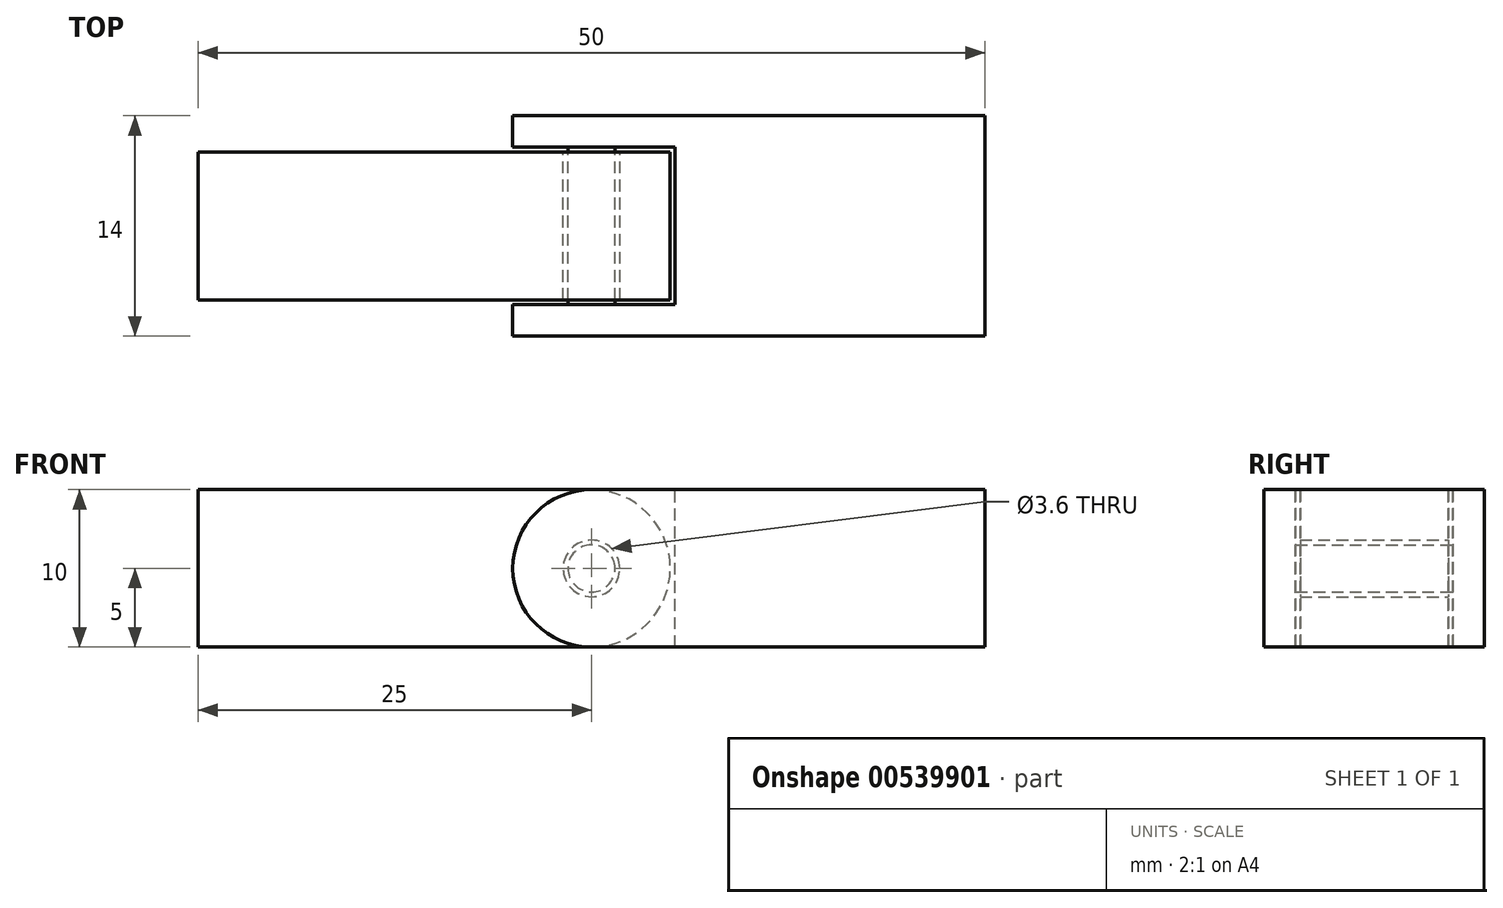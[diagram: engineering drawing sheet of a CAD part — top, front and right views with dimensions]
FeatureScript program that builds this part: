
annotation { "Feature Type Name" : "Feature", "Feature Type Description" : "" }
export const myFeature = defineFeature(function(context is Context, id is Id, definition is map)
    precondition{}
    {
        {
            var Q0;
            Q0=qCreatedBy(makeId("Front.planeOp"),FACE);
            var sketch = newSketch(context, id + "F0", { "sketchPlane" : qUnion([Q0])});
            skLineSegment(sketch, "E0.bottom", {"start": v(0, 0) * mm, "end": v(-25, 0) * mm});
            skLineSegment(sketch, "E0.top", {"start": v(0, 10) * mm, "end": v(-25, 10) * mm});
            skLineSegment(sketch, "E0.left", {"start": v(0, 0) * mm, "end": v(0, 10) * mm});
            skLineSegment(sketch, "E0.right", {"start": v(-30, 5) * mm, "end": v(-30, 5) * mm});
            skPoint(sketch, "E1.visualSharp", {"position": v(-30, 10) * mm});
            skArc(sketch, "E1.filletArc", {"start": v(-25, 10) * mm, "mid": v(-28.54, 8.54) * mm, "end": v(-30, 5) * mm});
            skPoint(sketch, "E2.visualSharp", {"position": v(-30, 0) * mm});
            skArc(sketch, "E2.filletArc", {"start": v(-30, 5) * mm, "mid": v(-28.54, 1.46) * mm, "end": v(-25, 0) * mm});
            skLineSegment(sketch, "E3", {"start": v(-30, 5) * mm, "end": v(-11.95, 5) * mm, "construction": true});
            skLineSegment(sketch, "E4", {"start": v(-25, 10) * mm, "end": v(-25, -3.08) * mm, "construction": true});
            skSolve(sketch);
        }
        {
            var Q0;
            Q0 = qSketchRegion(id + "F0", true);
            extrude(context, id + "F1", {"entities" : qUnion([Q0]), "depth" : 14 * mm, "offsetDistance" : 25 * mm});
        }
        {
            var Q0;
            Q0=makeQuery(id+"F1.opExtrude","SWEPT_FACE",FACE,{"disambiguationData":[OSD([sQuery(id+"F0.wireOp",EDGE,"E0.top")])]});
            var sketch = newSketch(context, id + "F2", { "sketchPlane" : qUnion([Q0])});
            skLineSegment(sketch, "E5.bottom", {"start": v(-30.1, -2) * mm, "end": v(-19.7, -2) * mm});
            skLineSegment(sketch, "E5.top", {"start": v(-30.1, -12) * mm, "end": v(-19.7, -12) * mm});
            skLineSegment(sketch, "E5.left", {"start": v(-30.1, -2) * mm, "end": v(-30.1, -12) * mm});
            skLineSegment(sketch, "E6", {"start": v(-19.7, -2) * mm, "end": v(-19.7, -12) * mm});
            skSolve(sketch);
        }
        {
            var Q0;
            Q0 = qSketchRegion(id + "F2", true);
            extrude(context, id + "F3", {"entities" : qUnion([Q0]), "operationType" : NewBodyOperationType.REMOVE, "endBound" : BoundingType.THROUGH_ALL, "oppositeDirection" : true, "depth" : 25 * mm, "offsetDistance" : 25 * mm});
        }
        {
            var Q0;
            Q0=makeQuery(id+"F1.opExtrude","CAP_FACE",FACE,{"disambiguationData":[OSD([sQuery(id+"F0.wireOp",EDGE,"E0.bottom"),sQuery(id+"F0.wireOp",EDGE,"E0.top"),sQuery(id+"F0.wireOp",EDGE,"E0.left"),sQuery(id+"F0.wireOp",EDGE,"E1.filletArc"),sQuery(id+"F0.wireOp",EDGE,"E2.filletArc")])],"isStart":true});
            var sketch = newSketch(context, id + "F4", { "sketchPlane" : qUnion([Q0])});
            skCircle(sketch, "E7", {"center": v(25, 5) * mm, "radius": 1.5 * mm});
            skSolve(sketch);
        }
        {
            var Q0;
            Q0 = qSketchRegion(id + "F4", true);
            var Q1;
            Q1=makeQuery(id+"F3.boolean.opBoolean","COPY",FACE,{"derivedFrom":makeQuery(id+"F3.opExtrude","SWEPT_FACE",FACE,{"disambiguationData":[OSD([sQuery(id+"F2.wireOp",EDGE,"E5.top")])]})});
            extrude(context, id + "F5", {"entities" : qUnion([Q0]), "operationType" : NewBodyOperationType.ADD, "endBound" : BoundingType.UP_TO_SURFACE, "oppositeDirection" : true, "depth" : 25 * mm, "endBoundEntityFace" : qUnion([Q1]), "offsetDistance" : 25 * mm});
        }
        {
            var Q0;
            Q0=makeQuery(id+"F1.opExtrude","CAP_FACE",FACE,{"disambiguationData":[OSD([sQuery(id+"F0.wireOp",EDGE,"E0.bottom"),sQuery(id+"F0.wireOp",EDGE,"E0.top"),sQuery(id+"F0.wireOp",EDGE,"E0.left"),sQuery(id+"F0.wireOp",EDGE,"E1.filletArc"),sQuery(id+"F0.wireOp",EDGE,"E2.filletArc")])],"isStart":true});
            cPlane(context, id + "F6", {"entities" : qUnion([Q0]), "cplaneType" : CPlaneType.OFFSET, "offset" : 2.3 * mm, "oppositeDirection" : true, "width" : 150 * mm, "height" : 150 * mm});
        }
        {
            var Q0;
            Q0=qCreatedBy(id+"F6.planeOp",FACE);
            var sketch = newSketch(context, id + "F7", { "sketchPlane" : qUnion([Q0])});
            skCircle(sketch, "E8", {"center": v(25, 5) * mm, "radius": 1.8 * mm});
            skArc(sketch, "E9", {"start": v(25, 10) * mm, "mid": v(20, 5) * mm, "end": v(25, 0) * mm});
            skLineSegment(sketch, "E10.bottom", {"start": v(25, 0) * mm, "end": v(50, 0) * mm});
            skLineSegment(sketch, "E10.top", {"start": v(25, 10) * mm, "end": v(50, 10) * mm});
            skLineSegment(sketch, "E10.right", {"start": v(50, 0) * mm, "end": v(50, 10) * mm});
            skSolve(sketch);
        }
        {
            var Q0;
            Q0 = qSketchRegion(id + "F7", true);
            extrude(context, id + "F8", {"entities" : qUnion([Q0]), "oppositeDirection" : true, "depth" : 9.4 * mm, "offsetDistance" : 25 * mm});
        }
    });
